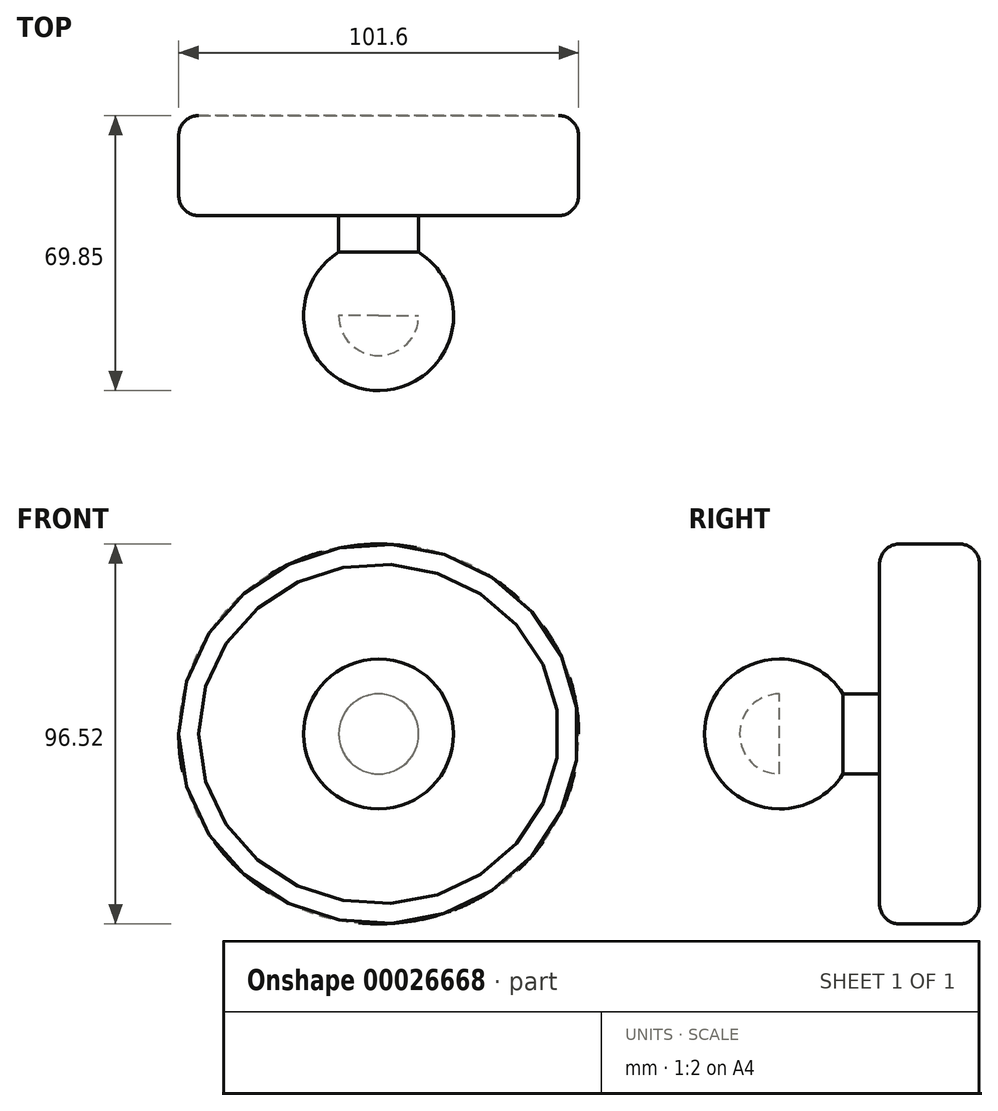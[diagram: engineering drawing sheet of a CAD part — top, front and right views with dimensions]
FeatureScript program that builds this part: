
annotation { "Feature Type Name" : "Feature", "Feature Type Description" : "" }
export const myFeature = defineFeature(function(context is Context, id is Id, definition is map)
    precondition{}
    {
        {
            var Q0;
            Q0=qCreatedBy(makeId("Front.planeOp"),FACE);
            var sketch = newSketch(context, id + "F0", { "sketchPlane" : qUnion([Q0])});
            skEllipse(sketch, "E0", {"center": v(0, 0) * mm, "majorRadius": 48.26 * mm, "minorRadius": 50.8 * mm, "majorAxis": v(0, 1)});
            skSolve(sketch);
        }
        {
            var Q0;
            Q0 = qSketchRegion(id + "F0", true);
            extrude(context, id + "F1", {"entities" : qUnion([Q0]), "depth" : 25.4 * mm});
        }
        {
            var Q0;
            Q0=makeQuery(id+"F1.opExtrude","CAP_EDGE",EDGE,{"disambiguationData":[OSD([sQuery(id+"F0.wireOp",EDGE,"E0")])],"isStart":false});
            var Q1;
            Q1=makeQuery(id+"F1.opExtrude","CAP_EDGE",EDGE,{"disambiguationData":[OSD([sQuery(id+"F0.wireOp",EDGE,"E0")])],"isStart":true});
            fillet(context, id + "F2", {"entities" : qUnion([Q0, Q1]), "radius" : 5.08 * mm, "tangentPropagation" : true, "allowEdgeOverflow" : false});
        }
        {
            var Q0;
            Q0=makeQuery(id+"F1.opExtrude","CAP_FACE",FACE,{"disambiguationData":[OSD([sQuery(id+"F0.wireOp",EDGE,"E0")])],"isStart":false});
            var sketch = newSketch(context, id + "F3", { "sketchPlane" : qUnion([Q0])});
            skCircle(sketch, "E1", {"center": v(0, 0) * mm, "radius": 10.16 * mm});
            skSolve(sketch);
        }
        {
            var Q0;
            Q0 = qSketchRegion(id + "F3", true);
            extrude(context, id + "F4", {"entities" : qUnion([Q0]), "operationType" : NewBodyOperationType.ADD, "depth" : 25.4 * mm});
        }
        {
            var Q0;
            Q0=makeQuery(id+"F4.opExtrude","CAP_FACE",FACE,{"disambiguationData":[OSD([sQuery(id+"F3.wireOp",EDGE,"E1")])],"isStart":false});
            var sketch = newSketch(context, id + "F5", { "sketchPlane" : qUnion([Q0])});
            skCircle(sketch, "E2", {"center": v(0, 0) * mm, "radius": 19.05 * mm});
            skLineSegment(sketch, "E3", {"start": v(0, 19.05) * mm, "end": v(0, -19.05) * mm});
            skSolve(sketch);
        }
        {
            var Q0;
            {var subQ0=sQuery(id+"F5.wireOp",EDGE,"E3");Q0=makeQuery(id+"F5.imprint","IMPRINT",FACE,{"disambiguationData":[TD([[makeQuery(id+"F5.imprint","IMPRINT",EDGE,{"derivedFrom":subQ0}),1.0]])]});}
            var Q1;
            Q1=sQuery(id+"F5.wireOp",EDGE,"E3");
            revolve(context, id + "F6", {"operationType" : NewBodyOperationType.ADD, "entities" : qUnion([Q0]), "axis" : qUnion([Q1]), "revolveType" : RevolveType.FULL});
        }
    });
